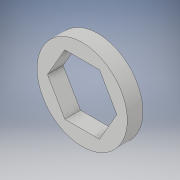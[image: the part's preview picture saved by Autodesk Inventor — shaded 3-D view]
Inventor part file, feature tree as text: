
AUTODESK INVENTOR PART (.ipt)
format: ipt  version: 2018 (Build 220112000, 112)  size: 103,936 bytes
history: native  units: in
note: dims shown in document units (in); Inventor stores cm internally (conversion verified against a paired STEP export)
features: extrude x1, sketch x1
ambient origin geometry x8: Origin, YZ Plane, XZ Plane, XY Plane, X Axis, Y Axis, Z Axis, Center Point
bodies: Solid1 (feature_tree)
feature tree (2):
  extrude  "Extrusion1"  Depth=0.13in
  sketch  "Sketch1"  dims[d0=0.75in d1=0.25in d2=0.13in d3=0.0in]
